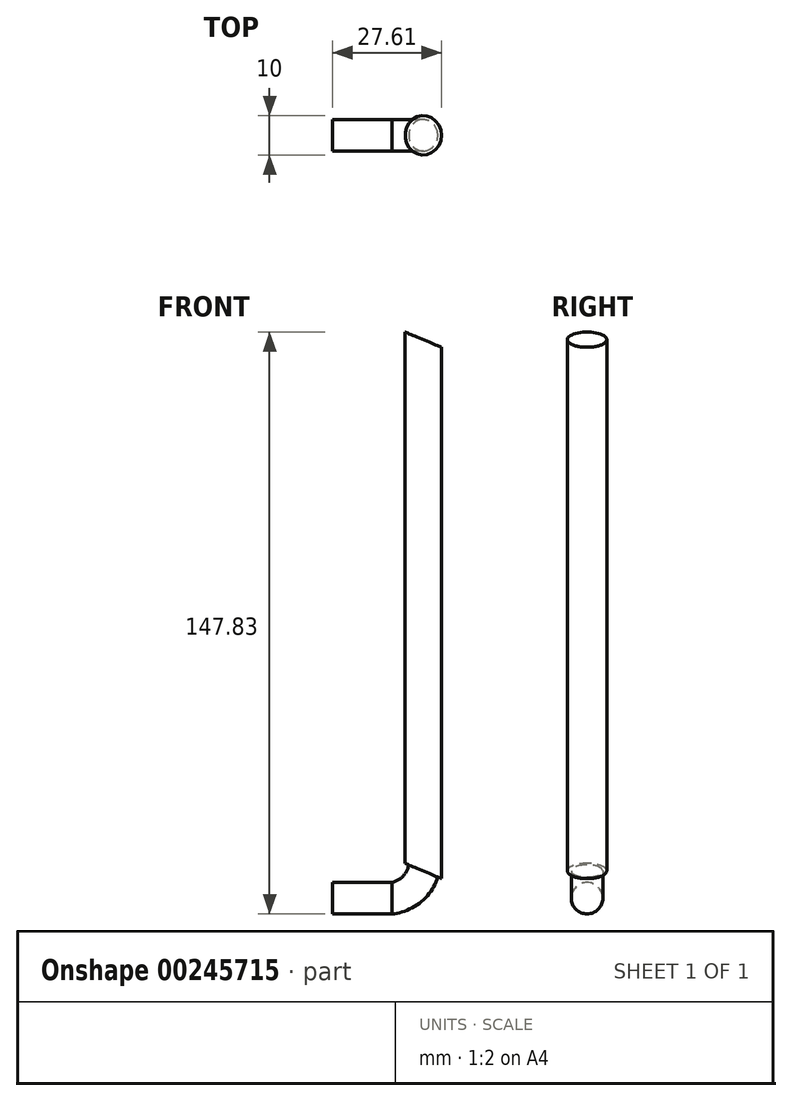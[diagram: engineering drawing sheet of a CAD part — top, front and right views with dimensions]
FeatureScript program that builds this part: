
annotation { "Feature Type Name" : "Feature", "Feature Type Description" : "" }
export const myFeature = defineFeature(function(context is Context, id is Id, definition is map)
    precondition{}
    {
        {
            var Q0;
            Q0=qCreatedBy(makeId("Right.planeOp"),FACE);
            var sketch = newSketch(context, id + "F0", { "sketchPlane" : qUnion([Q0])});
            skCircle(sketch, "E0", {"center": v(0, 0) * mm, "radius": 4 * mm});
            skSolve(sketch);
        }
        {
            var Q0;
            Q0=qCreatedBy(makeId("Front.planeOp"),FACE);
            var sketch = newSketch(context, id + "F1", { "sketchPlane" : qUnion([Q0])});
            skArc(sketch, "E1", {"start": v(0, 0) * mm, "mid": v(5.04, 2.24) * mm, "end": v(8, 6.9) * mm});
            skPoint(sketch, "E2", {"position": v(0, 8) * mm});
            skSolve(sketch);
        }
        {
            var Q0;
            Q0=makeQuery(id+"F0.imprint","IMPRINT",FACE,{"disambiguationData":[TD([[makeQuery(id+"F0.imprint","IMPRINT",EDGE,{"derivedFrom":sQuery(id+"F0.wireOp",EDGE,"E0")}),1.0]])]});
            var Q1;
            Q1=sQuery(id+"F1.wireOp",EDGE,"E1");
            sweep(context, id + "F2", {"profiles" : qUnion([Q0]), "path" : qUnion([Q1])});
        }
        {
            var Q0;
            Q0=makeQuery(id+"F2.opSweep","CAP_FACE",FACE,{"disambiguationData":[OSD([sQuery(id+"F0.wireOp",EDGE,"E0"),sQuery(id+"F1.wireOp",VERTEX,"E1.end")])],"isStart":false});
            var sketch = newSketch(context, id + "F3", { "sketchPlane" : qUnion([Q0])});
            skCircle(sketch, "E3", {"center": v(4.73, 0) * mm, "radius": 5 * mm});
            skSolve(sketch);
        }
        {
            var Q0;
            Q0=makeQuery(id+"F2.opSweep","CAP_FACE",FACE,{"disambiguationData":[OSD([sQuery(id+"F0.wireOp",EDGE,"E0"),sQuery(id+"F1.wireOp",VERTEX,"E1.end")])],"isStart":false});
            var sketch = newSketch(context, id + "F4", { "sketchPlane" : qUnion([Q0])});
            skCircle(sketch, "E4.0", {"center": v(4.73, 0) * mm, "radius": 4 * mm});
            skLineSegment(sketch, "E5", {"start": v(8.73, 0) * mm, "end": v(8.47, -1.4) * mm});
            skLineSegment(sketch, "E6.bottom", {"start": v(8.73, 0) * mm, "end": v(11, 0) * mm});
            skLineSegment(sketch, "E6.top", {"start": v(8.73, 3.96) * mm, "end": v(11, 3.96) * mm});
            skLineSegment(sketch, "E6.left", {"start": v(8.73, 0) * mm, "end": v(8.73, 3.96) * mm});
            skLineSegment(sketch, "E6.right", {"start": v(11, 0) * mm, "end": v(11, 3.96) * mm});
            skLineSegment(sketch, "E7.top", {"start": v(8.73, -4.42) * mm, "end": v(11, -4.42) * mm});
            skLineSegment(sketch, "E7.left", {"start": v(8.73, 0) * mm, "end": v(8.73, -4.42) * mm});
            skLineSegment(sketch, "E7.right", {"start": v(11, 0) * mm, "end": v(11, -4.42) * mm});
            skSolve(sketch);
        }
        {
            var Q0;
            Q0=qCreatedBy(makeId("Front.planeOp"),FACE);
            var sketch = newSketch(context, id + "F5", { "sketchPlane" : qUnion([Q0])});
            skLineSegment(sketch, "E8", {"start": v(8, 6.9) * mm, "end": v(8, 141.9) * mm});
            skLineSegment(sketch, "E9.0", {"start": v(4.3, 8.44) * mm, "end": v(11.7, 5.36) * mm});
            skArc(sketch, "E10", {"start": v(37.7, 164.73) * mm, "mid": v(17.23, 160.63) * mm, "end": v(8, 141.9) * mm});
            skSolve(sketch);
        }
        {
            var Q0;
            Q0=makeQuery(id+"F3.imprint","IMPRINT",FACE,{"disambiguationData":[TD([[makeQuery(id+"F3.imprint","IMPRINT",EDGE,{"derivedFrom":makeQuery(id+"F2.opSweep","CAP_EDGE",EDGE,{"disambiguationData":[OSD([sQuery(id+"F0.wireOp",EDGE,"E0"),sQuery(id+"F1.wireOp",VERTEX,"E1.end")])],"isStart":false})}),1.0]])]});
            var Q1;
            Q1=makeQuery(id+"F3.imprint","IMPRINT",FACE,{"disambiguationData":[TD([[makeQuery(id+"F3.imprint","IMPRINT",EDGE,{"derivedFrom":sQuery(id+"F3.wireOp",EDGE,"E3")}),1.0]])]});
            var Q2;
            Q2=sQuery(id+"F5.wireOp",EDGE,"E8");
            sweep(context, id + "F6", {"operationType" : NewBodyOperationType.ADD, "profiles" : qUnion([Q0, Q1]), "path" : qUnion([Q2])});
        }
        {
            var Q0;
            Q0=makeQuery(id+"F2.opSweep","CAP_FACE",FACE,{"disambiguationData":[OSD([sQuery(id+"F0.wireOp",EDGE,"E0"),sQuery(id+"F1.wireOp",VERTEX,"E1.start")])],"isStart":true});
            extrude(context, id + "F7", {"entities" : qUnion([Q0]), "operationType" : NewBodyOperationType.ADD, "depth" : 15 * mm});
        }
    });
